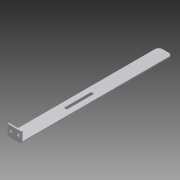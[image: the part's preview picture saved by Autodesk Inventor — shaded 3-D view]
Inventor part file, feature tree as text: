
AUTODESK INVENTOR PART (.ipt)
format: ipt  version: 2015 (Build 190159000, 159)  size: 131,072 bytes
history: native  units: mm
features: sketch x4, extrude x3, other x1, hole x1, fillet x1
ambient origin geometry x8: Origin, YZ Plane, XZ Plane, XY Plane, X Axis, Y Axis, Z Axis, Center Point
bodies: Body1 (feature_tree)
feature tree (10):
  other  "ソリッド1"
  extrude  "押し出し1"  Depth=15.0mm
  extrude  "押し出し2"  Depth=166.0mm
  extrude  "押し出し3"  Depth=1.5mm TaperAngle=0.0deg
  hole  "穴1"  [1 undecoded]
  fillet  "フィレット1"  Radius=30.0mm
  sketch  "スケッチ1"
  sketch  "スケッチ2"
  sketch  "スケッチ3"
  sketch  "スケッチ4"
note: 1 required parameter value undecoded (feature->parameter linkage not recoverable at this tier; creation-order binding heuristic only, values carry confidence <= 0.55)
